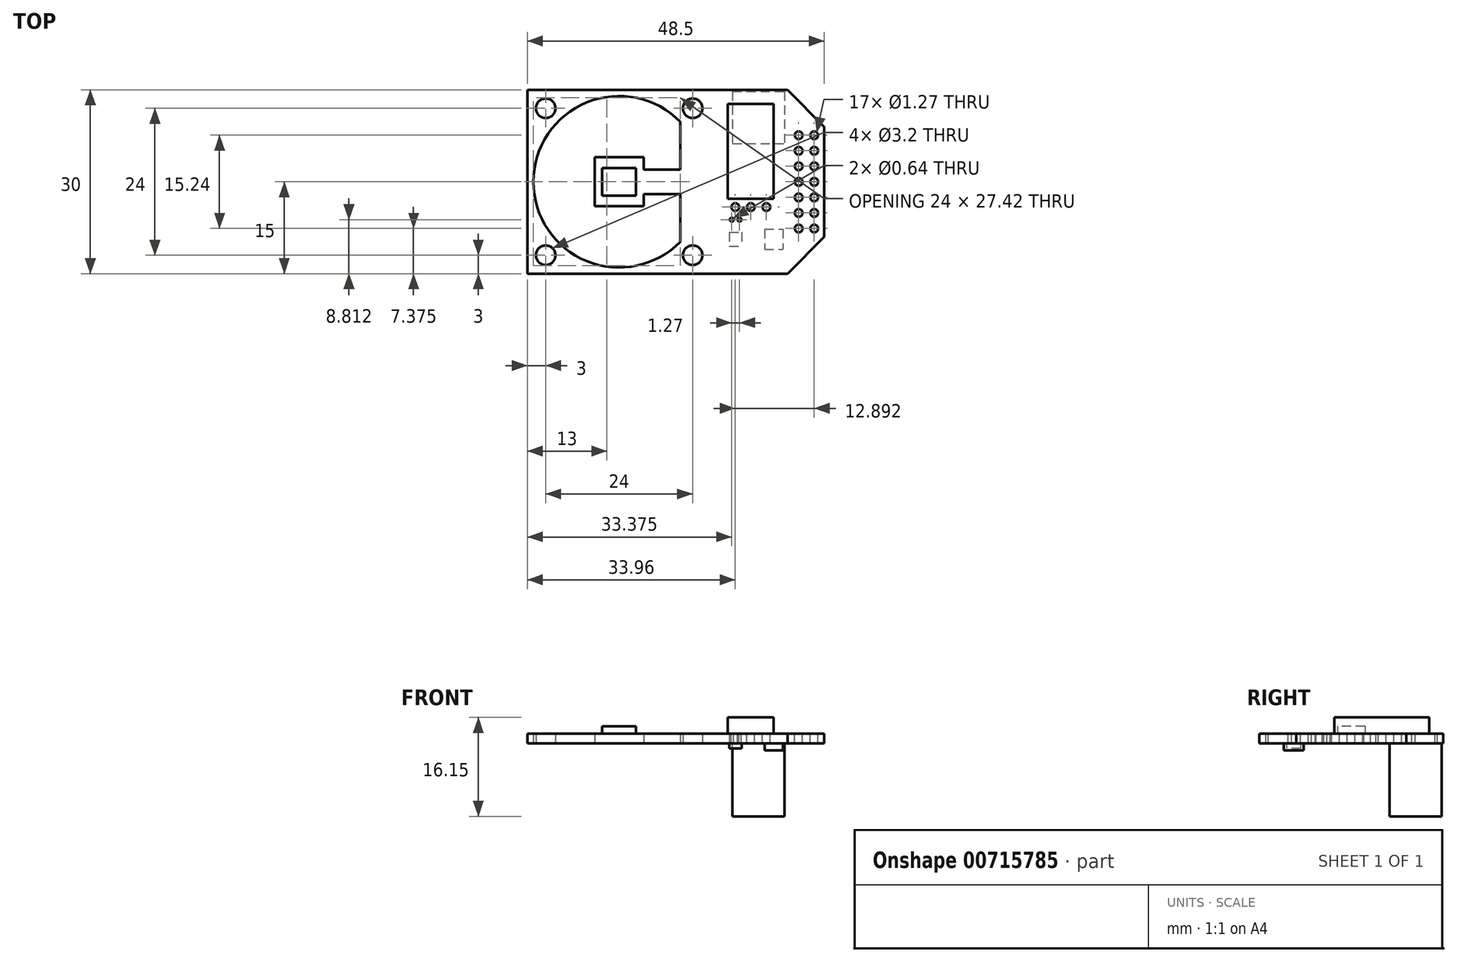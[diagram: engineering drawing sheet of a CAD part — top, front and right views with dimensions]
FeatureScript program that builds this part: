
annotation { "Feature Type Name" : "Feature", "Feature Type Description" : "" }
export const myFeature = defineFeature(function(context is Context, id is Id, definition is map)
    precondition{}
    {
        {
            var Q0;
            Q0=qCreatedBy(makeId("Top.planeOp"),FACE);
            var sketch = newSketch(context, id + "F0", { "sketchPlane" : qUnion([Q0])});
            skLineSegment(sketch, "E0", {"start": v(-15, -15) * mm, "end": v(-15, 15) * mm});
            skLineSegment(sketch, "E1", {"start": v(-15, 15) * mm, "end": v(27.5, 15) * mm});
            skLineSegment(sketch, "E2", {"start": v(27.5, 15) * mm, "end": v(33.5, 9) * mm});
            skLineSegment(sketch, "E3", {"start": v(33.5, 9) * mm, "end": v(33.5, -9) * mm});
            skLineSegment(sketch, "E4", {"start": v(33.5, -9) * mm, "end": v(27.5, -15) * mm});
            skLineSegment(sketch, "E5", {"start": v(27.5, -15) * mm, "end": v(-15, -15) * mm});
            skPoint(sketch, "E6", {"position": v(33.5, 0) * mm});
            skLineSegment(sketch, "E7.bottom", {"start": v(12, 12) * mm, "end": v(-12, 12) * mm, "construction": true});
            skLineSegment(sketch, "E7.top", {"start": v(12, -12) * mm, "end": v(-12, -12) * mm, "construction": true});
            skLineSegment(sketch, "E7.left", {"start": v(12, 12) * mm, "end": v(12, -12) * mm, "construction": true});
            skLineSegment(sketch, "E7.right", {"start": v(-12, 12) * mm, "end": v(-12, -12) * mm, "construction": true});
            skPoint(sketch, "E7.middle", {"position": v(0, 0) * mm});
            skCircle(sketch, "E8", {"center": v(-12, 12) * mm, "radius": 1.6 * mm});
            skCircle(sketch, "E9", {"center": v(12, 12) * mm, "radius": 1.6 * mm});
            skCircle(sketch, "E10", {"center": v(12, -12) * mm, "radius": 1.6 * mm});
            skCircle(sketch, "E11", {"center": v(-12, -12) * mm, "radius": 1.6 * mm});
            skLineSegment(sketch, "E12.bottom", {"start": v(4, 4) * mm, "end": v(-4, 4) * mm});
            skLineSegment(sketch, "E12.top", {"start": v(4, -4) * mm, "end": v(-4, -4) * mm});
            skLineSegment(sketch, "E12.left", {"start": v(4, 4) * mm, "end": v(4, -4) * mm});
            skLineSegment(sketch, "E12.right", {"start": v(-4, 4) * mm, "end": v(-4, -4) * mm});
            skLineSegment(sketch, "E13.bottom", {"start": v(14, 2) * mm, "end": v(4, 2) * mm});
            skLineSegment(sketch, "E13.top", {"start": v(14, -2) * mm, "end": v(4, -2) * mm});
            skLineSegment(sketch, "E13.left", {"start": v(14, 2) * mm, "end": v(14, -2) * mm});
            skLineSegment(sketch, "E13.right", {"start": v(4, 2) * mm, "end": v(4, -2) * mm});
            skPoint(sketch, "E13.middle", {"position": v(9, 0) * mm});
            skCircle(sketch, "E14", {"center": v(0, 0) * mm, "radius": 14 * mm});
            skLineSegment(sketch, "E15", {"start": v(10, 9.8) * mm, "end": v(10, -9.8) * mm});
            skSolve(sketch);
        }
        {
            var Q0;
            {var subQ0=sQuery(id+"F0.wireOp",EDGE,"E13.bottom");var subQ1=sQuery(id+"F0.wireOp",EDGE,"E12.left");var subQ2=makeQuery(id+"F0.imprint","INTERSECT",VERTEX,{"derivedFrom":[subQ1,subQ0]});Q0=makeQuery(id+"F0.imprint","IMPRINT",FACE,{"disambiguationData":[TD([[makeQuery(id+"F0.imprint","IMPRINT",EDGE,{"disambiguationData":[TD([[subQ2,-1.0]])],"derivedFrom":subQ1}),1.0]])]});}
            var Q1;
            {var subQ4=sQuery(id+"F0.wireOp",EDGE,"E15");var subQ5=sQuery(id+"F0.wireOp",EDGE,"E13.bottom");var subQ6=makeQuery(id+"F0.imprint","INTERSECT",VERTEX,{"derivedFrom":[subQ5,subQ4]});Q1=makeQuery(id+"F0.imprint","IMPRINT",FACE,{"disambiguationData":[TD([[makeQuery(id+"F0.imprint","IMPRINT",EDGE,{"disambiguationData":[TD([[subQ6,1.0]])],"derivedFrom":subQ5}),1.0]])]});}
            var Q2;
            Q2=makeQuery(id+"F0.imprint","IMPRINT",FACE,{"disambiguationData":[TD([[makeQuery(id+"F0.imprint","IMPRINT",EDGE,{"derivedFrom":sQuery(id+"F0.wireOp",EDGE,"E0")}),-1.0]])]});
            var Q3;
            {var subQ0=sQuery(id+"F0.wireOp",EDGE,"E14");var subQ1=sQuery(id+"F0.wireOp",EDGE,"E13.bottom");var subQ2=makeQuery(id+"F0.imprint","INTERSECT",VERTEX,{"derivedFrom":[subQ1,subQ0]});Q3=makeQuery(id+"F0.imprint","IMPRINT",FACE,{"disambiguationData":[TD([[makeQuery(id+"F0.imprint","IMPRINT",EDGE,{"disambiguationData":[TD([[subQ2,1.0]])],"derivedFrom":subQ1}),1.0]])]});}
            var Q4;
            {var subQ0=sQuery(id+"F0.wireOp",EDGE,"E14");var subQ1=sQuery(id+"F0.wireOp",EDGE,"E13.top");var subQ2=makeQuery(id+"F0.imprint","INTERSECT",VERTEX,{"derivedFrom":[subQ1,subQ0]});Q4=makeQuery(id+"F0.imprint","IMPRINT",FACE,{"disambiguationData":[TD([[makeQuery(id+"F0.imprint","IMPRINT",EDGE,{"disambiguationData":[TD([[subQ2,1.0]])],"derivedFrom":subQ1}),-1.0]])]});}
            var Q5;
            {var subQ4=sQuery(id+"F0.wireOp",EDGE,"E12.bottom");Q5=makeQuery(id+"F0.imprint","IMPRINT",FACE,{"disambiguationData":[TD([[makeQuery(id+"F0.imprint","IMPRINT",EDGE,{"derivedFrom":subQ4}),1.0]])]});}
            var Q6;
            {var subQ0=sQuery(id+"F0.wireOp",EDGE,"E15");var subQ1=sQuery(id+"F0.wireOp",EDGE,"E13.bottom");var subQ2=makeQuery(id+"F0.imprint","INTERSECT",VERTEX,{"derivedFrom":[subQ1,subQ0]});Q6=makeQuery(id+"F0.imprint","IMPRINT",FACE,{"disambiguationData":[TD([[makeQuery(id+"F0.imprint","IMPRINT",EDGE,{"disambiguationData":[TD([[subQ2,1.0]])],"derivedFrom":subQ1}),-1.0]])]});}
            var Q7;
            {var subQ0=sQuery(id+"F0.wireOp",EDGE,"E15");var subQ1=sQuery(id+"F0.wireOp",EDGE,"E13.top");var subQ2=makeQuery(id+"F0.imprint","INTERSECT",VERTEX,{"derivedFrom":[subQ1,subQ0]});Q7=makeQuery(id+"F0.imprint","IMPRINT",FACE,{"disambiguationData":[TD([[makeQuery(id+"F0.imprint","IMPRINT",EDGE,{"disambiguationData":[TD([[subQ2,1.0]])],"derivedFrom":subQ1}),1.0]])]});}
            extrude(context, id + "F1", {"entities" : qUnion([Q0, Q1, Q2, Q3, Q4, Q5, Q6, Q7]), "depth" : 1.6 * mm});
        }
        {
            var Q0;
            Q0=makeQuery(id+"F1.opExtrude","CAP_FACE",FACE,{"disambiguationData":[OSD([sQuery(id+"F0.wireOp",EDGE,"E0"),sQuery(id+"F0.wireOp",EDGE,"E1"),sQuery(id+"F0.wireOp",EDGE,"E2"),sQuery(id+"F0.wireOp",EDGE,"E3"),sQuery(id+"F0.wireOp",EDGE,"E4"),sQuery(id+"F0.wireOp",EDGE,"E5"),sQuery(id+"F0.wireOp",EDGE,"E8"),sQuery(id+"F0.wireOp",EDGE,"E9"),sQuery(id+"F0.wireOp",EDGE,"E10"),sQuery(id+"F0.wireOp",EDGE,"E11"),sQuery(id+"F0.wireOp",EDGE,"E12.bottom"),sQuery(id+"F0.wireOp",EDGE,"E12.top"),sQuery(id+"F0.wireOp",EDGE,"E12.left"),sQuery(id+"F0.wireOp",EDGE,"E12.right"),sQuery(id+"F0.wireOp",EDGE,"E13.bottom"),sQuery(id+"F0.wireOp",EDGE,"E13.top"),sQuery(id+"F0.wireOp",EDGE,"E14"),sQuery(id+"F0.wireOp",EDGE,"E15")])],"isStart":false});
            var sketch = newSketch(context, id + "F2", { "sketchPlane" : qUnion([Q0])});
            skLineSegment(sketch, "E16.bottom", {"start": v(2.75, 2.25) * mm, "end": v(-2.75, 2.25) * mm});
            skLineSegment(sketch, "E16.top", {"start": v(2.75, -2.25) * mm, "end": v(-2.75, -2.25) * mm});
            skLineSegment(sketch, "E16.left", {"start": v(2.75, 2.25) * mm, "end": v(2.75, -2.25) * mm});
            skLineSegment(sketch, "E16.right", {"start": v(-2.75, 2.25) * mm, "end": v(-2.75, -2.25) * mm});
            skPoint(sketch, "E16.middle", {"position": v(0, 0) * mm});
            skLineSegment(sketch, "E17.bottom", {"start": v(25.25, 12.75) * mm, "end": v(17.75, 12.75) * mm});
            skLineSegment(sketch, "E17.top", {"start": v(25.25, -2.75) * mm, "end": v(17.75, -2.75) * mm});
            skLineSegment(sketch, "E17.left", {"start": v(25.25, 12.75) * mm, "end": v(25.25, -2.75) * mm});
            skLineSegment(sketch, "E17.right", {"start": v(17.75, 12.75) * mm, "end": v(17.75, -2.75) * mm});
            skPoint(sketch, "E17.middle", {"position": v(21.5, 5) * mm});
            skCircle(sketch, "E18", {"center": v(18.96, -4.13) * mm, "radius": 0.64 * mm});
            skCircle(sketch, "E19", {"center": v(21.5, -4.13) * mm, "radius": 0.64 * mm});
            skCircle(sketch, "E20", {"center": v(24.04, -4.13) * mm, "radius": 0.64 * mm});
            skLineSegment(sketch, "E21", {"start": v(18.96, -4.13) * mm, "end": v(21.5, -4.13) * mm, "construction": true});
            skLineSegment(sketch, "E22", {"start": v(21.5, -4.13) * mm, "end": v(24.04, -4.13) * mm, "construction": true});
            skCircle(sketch, "E23", {"center": v(29.31, 7.61) * mm, "radius": 0.64 * mm});
            skCircle(sketch, "E24.1.0.0", {"center": v(29.31, 5.07) * mm, "radius": 0.64 * mm});
            skCircle(sketch, "E24.2.0.0", {"center": v(29.31, 2.53) * mm, "radius": 0.64 * mm});
            skCircle(sketch, "E24.3.0.0", {"center": v(29.31, 0) * mm, "radius": 0.64 * mm});
            skCircle(sketch, "E24.4.0.0", {"center": v(29.31, -2.55) * mm, "radius": 0.64 * mm});
            skCircle(sketch, "E24.5.0.0", {"center": v(29.31, -5.09) * mm, "radius": 0.64 * mm});
            skCircle(sketch, "E24.6.0.0", {"center": v(29.31, -7.63) * mm, "radius": 0.64 * mm});
            skLineSegment(sketch, "E24.direction1", {"start": v(29.31, 7.61) * mm, "end": v(29.31, 5.07) * mm, "construction": true});
            skCircle(sketch, "E25.1.0.0", {"center": v(31.85, -2.55) * mm, "radius": 0.64 * mm});
            skCircle(sketch, "E25.1.0.1", {"center": v(31.85, 7.61) * mm, "radius": 0.64 * mm});
            skCircle(sketch, "E25.1.0.2", {"center": v(31.85, 5.07) * mm, "radius": 0.64 * mm});
            skCircle(sketch, "E25.1.0.3", {"center": v(31.85, 2.53) * mm, "radius": 0.64 * mm});
            skCircle(sketch, "E25.1.0.4", {"center": v(31.85, -7.63) * mm, "radius": 0.64 * mm});
            skCircle(sketch, "E25.1.0.5", {"center": v(31.85, 0) * mm, "radius": 0.64 * mm});
            skCircle(sketch, "E25.1.0.6", {"center": v(31.85, -5.09) * mm, "radius": 0.64 * mm});
            skLineSegment(sketch, "E25.1.0.7", {"start": v(31.85, 7.61) * mm, "end": v(31.85, 5.07) * mm, "construction": true});
            skLineSegment(sketch, "E25.direction1", {"start": v(29.31, -7.63) * mm, "end": v(31.85, -7.63) * mm, "construction": true});
            skCircle(sketch, "E26", {"center": v(18.38, -6.19) * mm, "radius": 0.32 * mm});
            skCircle(sketch, "E27", {"center": v(19.65, -6.19) * mm, "radius": 0.32 * mm});
            skSolve(sketch);
        }
        {
            var Q0;
            Q0=makeQuery(id+"F2.imprint","IMPRINT",FACE,{"disambiguationData":[TD([[makeQuery(id+"F2.imprint","IMPRINT",EDGE,{"derivedFrom":sQuery(id+"F2.wireOp",EDGE,"E16.bottom")}),1.0]])]});
            extrude(context, id + "F3", {"entities" : qUnion([Q0]), "operationType" : NewBodyOperationType.ADD, "depth" : 1.2 * mm});
        }
        {
            var Q0;
            Q0=makeQuery(id+"F2.imprint","IMPRINT",FACE,{"disambiguationData":[TD([[makeQuery(id+"F2.imprint","IMPRINT",EDGE,{"derivedFrom":sQuery(id+"F2.wireOp",EDGE,"E17.bottom")}),1.0]])]});
            extrude(context, id + "F4", {"entities" : qUnion([Q0]), "operationType" : NewBodyOperationType.ADD, "depth" : 2.65 * mm});
        }
        {
            var Q0;
            Q0=makeQuery(id+"F2.imprint","IMPRINT",FACE,{"disambiguationData":[TD([[makeQuery(id+"F2.imprint","IMPRINT",EDGE,{"derivedFrom":sQuery(id+"F2.wireOp",EDGE,"E18")}),1.0]])]});
            var Q1;
            Q1=makeQuery(id+"F2.imprint","IMPRINT",FACE,{"disambiguationData":[TD([[makeQuery(id+"F2.imprint","IMPRINT",EDGE,{"derivedFrom":sQuery(id+"F2.wireOp",EDGE,"E19")}),1.0]])]});
            var Q2;
            Q2=makeQuery(id+"F2.imprint","IMPRINT",FACE,{"disambiguationData":[TD([[makeQuery(id+"F2.imprint","IMPRINT",EDGE,{"derivedFrom":sQuery(id+"F2.wireOp",EDGE,"E20")}),1.0]])]});
            var Q3;
            Q3=makeQuery(id+"F2.imprint","IMPRINT",FACE,{"disambiguationData":[TD([[makeQuery(id+"F2.imprint","IMPRINT",EDGE,{"derivedFrom":sQuery(id+"F2.wireOp",EDGE,"E27")}),1.0]])]});
            var Q4;
            Q4=makeQuery(id+"F2.imprint","IMPRINT",FACE,{"disambiguationData":[TD([[makeQuery(id+"F2.imprint","IMPRINT",EDGE,{"derivedFrom":sQuery(id+"F2.wireOp",EDGE,"E26")}),1.0]])]});
            var Q5;
            Q5=makeQuery(id+"F2.imprint","IMPRINT",FACE,{"disambiguationData":[TD([[makeQuery(id+"F2.imprint","IMPRINT",EDGE,{"derivedFrom":sQuery(id+"F2.wireOp",EDGE,"E24.6.0.0")}),1.0]])]});
            var Q6;
            Q6=makeQuery(id+"F2.imprint","IMPRINT",FACE,{"disambiguationData":[TD([[makeQuery(id+"F2.imprint","IMPRINT",EDGE,{"derivedFrom":sQuery(id+"F2.wireOp",EDGE,"E25.1.0.4")}),1.0]])]});
            var Q7;
            Q7=makeQuery(id+"F2.imprint","IMPRINT",FACE,{"disambiguationData":[TD([[makeQuery(id+"F2.imprint","IMPRINT",EDGE,{"derivedFrom":sQuery(id+"F2.wireOp",EDGE,"E25.1.0.6")}),1.0]])]});
            var Q8;
            Q8=makeQuery(id+"F2.imprint","IMPRINT",FACE,{"disambiguationData":[TD([[makeQuery(id+"F2.imprint","IMPRINT",EDGE,{"derivedFrom":sQuery(id+"F2.wireOp",EDGE,"E24.5.0.0")}),1.0]])]});
            var Q9;
            Q9=makeQuery(id+"F2.imprint","IMPRINT",FACE,{"disambiguationData":[TD([[makeQuery(id+"F2.imprint","IMPRINT",EDGE,{"derivedFrom":sQuery(id+"F2.wireOp",EDGE,"E24.4.0.0")}),1.0]])]});
            var Q10;
            Q10=makeQuery(id+"F2.imprint","IMPRINT",FACE,{"disambiguationData":[TD([[makeQuery(id+"F2.imprint","IMPRINT",EDGE,{"derivedFrom":sQuery(id+"F2.wireOp",EDGE,"E25.1.0.0")}),1.0]])]});
            var Q11;
            Q11=makeQuery(id+"F2.imprint","IMPRINT",FACE,{"disambiguationData":[TD([[makeQuery(id+"F2.imprint","IMPRINT",EDGE,{"derivedFrom":sQuery(id+"F2.wireOp",EDGE,"E25.1.0.5")}),1.0]])]});
            var Q12;
            Q12=makeQuery(id+"F2.imprint","IMPRINT",FACE,{"disambiguationData":[TD([[makeQuery(id+"F2.imprint","IMPRINT",EDGE,{"derivedFrom":sQuery(id+"F2.wireOp",EDGE,"E24.3.0.0")}),1.0]])]});
            var Q13;
            Q13=makeQuery(id+"F2.imprint","IMPRINT",FACE,{"disambiguationData":[TD([[makeQuery(id+"F2.imprint","IMPRINT",EDGE,{"derivedFrom":sQuery(id+"F2.wireOp",EDGE,"E24.2.0.0")}),1.0]])]});
            var Q14;
            Q14=makeQuery(id+"F2.imprint","IMPRINT",FACE,{"disambiguationData":[TD([[makeQuery(id+"F2.imprint","IMPRINT",EDGE,{"derivedFrom":sQuery(id+"F2.wireOp",EDGE,"E25.1.0.3")}),1.0]])]});
            var Q15;
            Q15=makeQuery(id+"F2.imprint","IMPRINT",FACE,{"disambiguationData":[TD([[makeQuery(id+"F2.imprint","IMPRINT",EDGE,{"derivedFrom":sQuery(id+"F2.wireOp",EDGE,"E25.1.0.2")}),1.0]])]});
            var Q16;
            Q16=makeQuery(id+"F2.imprint","IMPRINT",FACE,{"disambiguationData":[TD([[makeQuery(id+"F2.imprint","IMPRINT",EDGE,{"derivedFrom":sQuery(id+"F2.wireOp",EDGE,"E24.1.0.0")}),1.0]])]});
            var Q17;
            Q17=makeQuery(id+"F2.imprint","IMPRINT",FACE,{"disambiguationData":[TD([[makeQuery(id+"F2.imprint","IMPRINT",EDGE,{"derivedFrom":sQuery(id+"F2.wireOp",EDGE,"E23")}),1.0]])]});
            var Q18;
            Q18=makeQuery(id+"F2.imprint","IMPRINT",FACE,{"disambiguationData":[TD([[makeQuery(id+"F2.imprint","IMPRINT",EDGE,{"derivedFrom":sQuery(id+"F2.wireOp",EDGE,"E25.1.0.1")}),1.0]])]});
            extrude(context, id + "F5", {"entities" : qUnion([Q0, Q1, Q2, Q3, Q4, Q5, Q6, Q7, Q8, Q9, Q10, Q11, Q12, Q13, Q14, Q15, Q16, Q17, Q18]), "operationType" : NewBodyOperationType.REMOVE, "oppositeDirection" : true, "depth" : 25 * mm});
        }
        {
            var Q0;
            Q0=makeQuery(id+"F1.opExtrude","CAP_FACE",FACE,{"disambiguationData":[OSD([sQuery(id+"F0.wireOp",EDGE,"E0"),sQuery(id+"F0.wireOp",EDGE,"E1"),sQuery(id+"F0.wireOp",EDGE,"E2"),sQuery(id+"F0.wireOp",EDGE,"E3"),sQuery(id+"F0.wireOp",EDGE,"E4"),sQuery(id+"F0.wireOp",EDGE,"E5"),sQuery(id+"F0.wireOp",EDGE,"E8"),sQuery(id+"F0.wireOp",EDGE,"E9"),sQuery(id+"F0.wireOp",EDGE,"E10"),sQuery(id+"F0.wireOp",EDGE,"E11"),sQuery(id+"F0.wireOp",EDGE,"E12.bottom"),sQuery(id+"F0.wireOp",EDGE,"E12.top"),sQuery(id+"F0.wireOp",EDGE,"E12.left"),sQuery(id+"F0.wireOp",EDGE,"E12.right"),sQuery(id+"F0.wireOp",EDGE,"E13.bottom"),sQuery(id+"F0.wireOp",EDGE,"E13.top"),sQuery(id+"F0.wireOp",EDGE,"E14"),sQuery(id+"F0.wireOp",EDGE,"E15")])],"isStart":true});
            var sketch = newSketch(context, id + "F6", { "sketchPlane" : qUnion([Q0])});
            skLineSegment(sketch, "E28.bottom", {"start": v(18.5, -14.75) * mm, "end": v(27, -14.75) * mm});
            skLineSegment(sketch, "E28.top", {"start": v(18.5, -6.25) * mm, "end": v(27, -6.25) * mm});
            skLineSegment(sketch, "E28.left", {"start": v(18.5, -14.75) * mm, "end": v(18.5, -6.25) * mm});
            skLineSegment(sketch, "E28.right", {"start": v(27, -14.75) * mm, "end": v(27, -6.25) * mm});
            skPoint(sketch, "E28.middle", {"position": v(22.75, -10.5) * mm});
            skLineSegment(sketch, "E29.bottom", {"start": v(23.75, 7.75) * mm, "end": v(26.75, 7.75) * mm});
            skLineSegment(sketch, "E29.top", {"start": v(23.75, 11) * mm, "end": v(26.75, 11) * mm});
            skLineSegment(sketch, "E29.left", {"start": v(23.75, 7.75) * mm, "end": v(23.75, 11) * mm});
            skLineSegment(sketch, "E29.right", {"start": v(26.75, 7.75) * mm, "end": v(26.75, 11) * mm});
            skPoint(sketch, "E29.middle", {"position": v(25.25, 9.38) * mm});
            skLineSegment(sketch, "E30.bottom", {"start": v(18, 8.25) * mm, "end": v(20, 8.25) * mm});
            skLineSegment(sketch, "E30.top", {"start": v(18, 10.5) * mm, "end": v(20, 10.5) * mm});
            skLineSegment(sketch, "E30.left", {"start": v(18, 8.25) * mm, "end": v(18, 10.5) * mm});
            skLineSegment(sketch, "E30.right", {"start": v(20, 8.25) * mm, "end": v(20, 10.5) * mm});
            skPoint(sketch, "E30.middle", {"position": v(19, 9.38) * mm});
            skSolve(sketch);
        }
        {
            var Q0;
            Q0=makeQuery(id+"F6.imprint","IMPRINT",FACE,{"disambiguationData":[TD([[makeQuery(id+"F6.imprint","IMPRINT",EDGE,{"derivedFrom":sQuery(id+"F6.wireOp",EDGE,"E28.bottom")}),1.0]])]});
            extrude(context, id + "F7", {"entities" : qUnion([Q0]), "operationType" : NewBodyOperationType.ADD, "depth" : 11.9 * mm});
        }
        {
            var Q0;
            Q0=makeQuery(id+"F6.imprint","IMPRINT",FACE,{"disambiguationData":[TD([[makeQuery(id+"F6.imprint","IMPRINT",EDGE,{"derivedFrom":sQuery(id+"F6.wireOp",EDGE,"E30.bottom")}),1.0]])]});
            extrude(context, id + "F8", {"entities" : qUnion([Q0]), "operationType" : NewBodyOperationType.ADD, "depth" : 0.8 * mm});
        }
        {
            var Q0;
            Q0=makeQuery(id+"F6.imprint","IMPRINT",FACE,{"disambiguationData":[TD([[makeQuery(id+"F6.imprint","IMPRINT",EDGE,{"derivedFrom":sQuery(id+"F6.wireOp",EDGE,"E29.bottom")}),1.0]])]});
            extrude(context, id + "F9", {"entities" : qUnion([Q0]), "operationType" : NewBodyOperationType.ADD, "depth" : 1.1 * mm});
        }
    });
